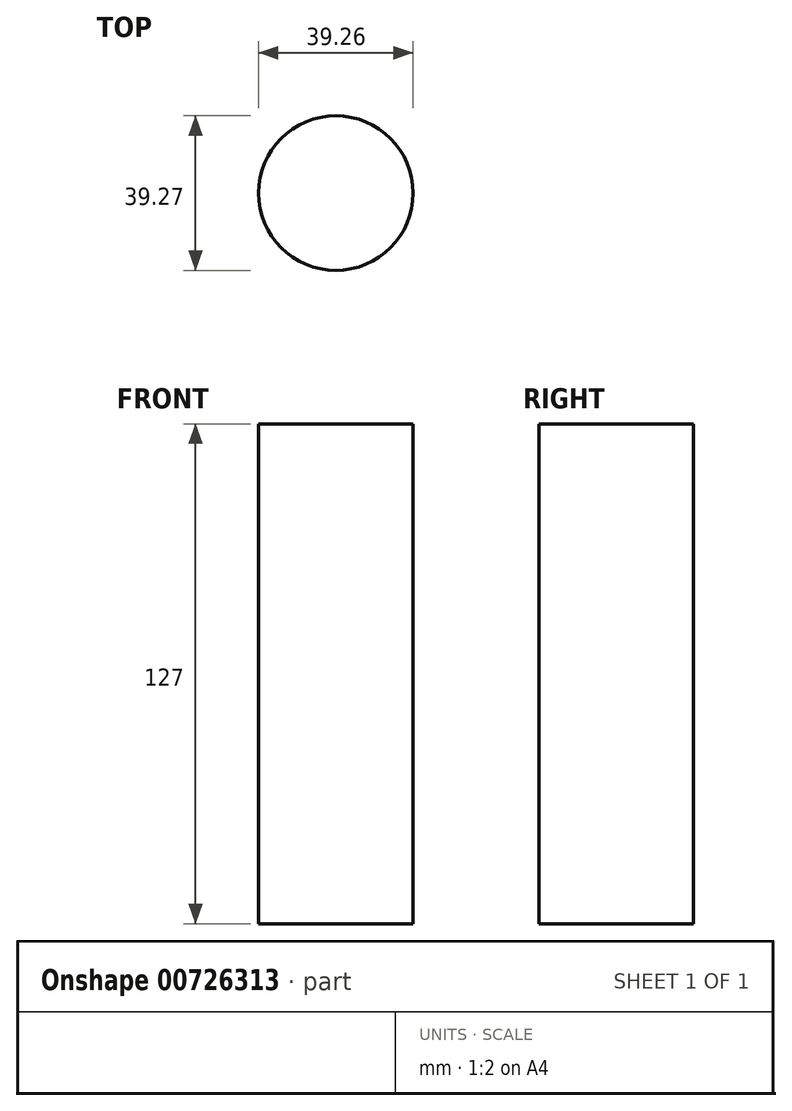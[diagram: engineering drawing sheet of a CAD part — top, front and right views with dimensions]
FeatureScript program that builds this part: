
annotation { "Feature Type Name" : "Feature", "Feature Type Description" : "" }
export const myFeature = defineFeature(function(context is Context, id is Id, definition is map)
    precondition{}
    {
        {
            var Q0;
            Q0=qCreatedBy(makeId("Top.planeOp"),FACE);
            var sketch = newSketch(context, id + "F0", { "sketchPlane" : qUnion([Q0])});
            skCircle(sketch, "E0", {"center": v(75.66, -70.47) * mm, "radius": 19.63 * mm});
            skSolve(sketch);
        }
        {
            var Q0;
            Q0 = qSketchRegion(id + "F0", true);
            extrude(context, id + "F1", {"entities" : qUnion([Q0]), "depth" : 127 * mm, "offsetDistance" : 25.4 * mm});
        }
    });
